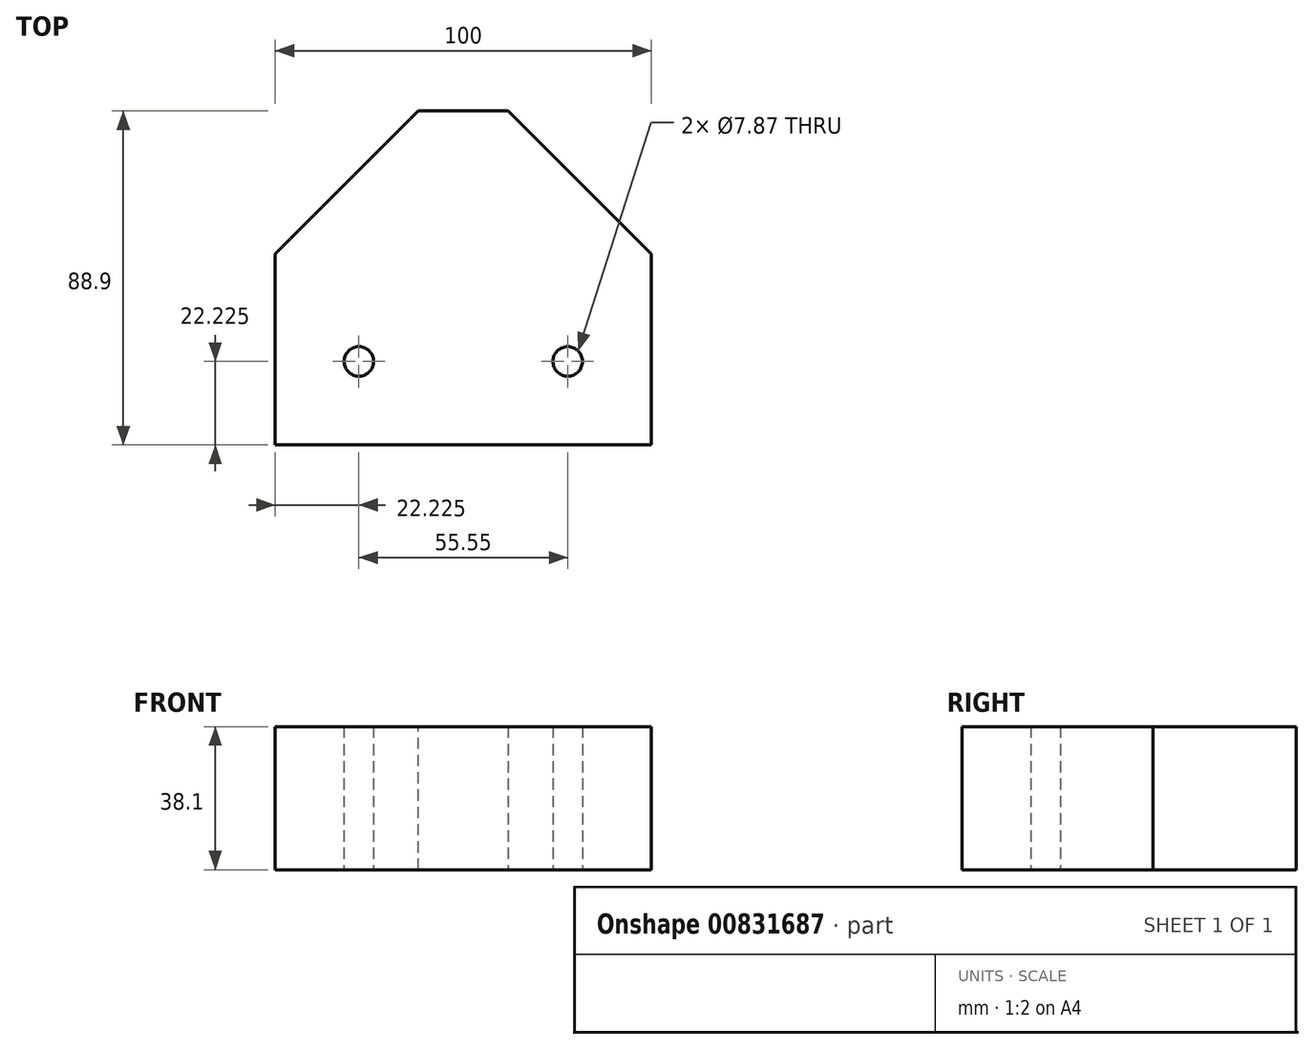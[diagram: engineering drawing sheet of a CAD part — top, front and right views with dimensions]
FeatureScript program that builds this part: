
annotation { "Feature Type Name" : "Feature", "Feature Type Description" : "" }
export const myFeature = defineFeature(function(context is Context, id is Id, definition is map)
    precondition{}
    {
        {
            var Q0;
            Q0=qCreatedBy(makeId("Top.planeOp"),FACE);
            var sketch = newSketch(context, id + "F0", { "sketchPlane" : qUnion([Q0])});
            skLineSegment(sketch, "E0.bottom", {"start": v(-50, 44.45) * mm, "end": v(50, 44.45) * mm});
            skLineSegment(sketch, "E0.top", {"start": v(-50, -44.45) * mm, "end": v(50, -44.45) * mm});
            skLineSegment(sketch, "E0.left", {"start": v(-50, 44.45) * mm, "end": v(-50, -44.45) * mm});
            skLineSegment(sketch, "E0.right", {"start": v(50, 44.45) * mm, "end": v(50, -44.45) * mm});
            skSolve(sketch);
        }
        {
            var Q0;
            Q0=makeQuery(id+"F0.imprint","IMPRINT",FACE,{"disambiguationData":[TD([[makeQuery(id+"F0.imprint","IMPRINT",EDGE,{"derivedFrom":sQuery(id+"F0.wireOp",EDGE,"E0.bottom")}),-1.0]])]});
            extrude(context, id + "F1", {"entities" : qUnion([Q0]), "depth" : 38.1 * mm, "offsetDistance" : 25.4 * mm});
        }
        {
            var Q0;
            Q0=makeQuery(id+"F1.opExtrude","SWEPT_EDGE",EDGE,{"disambiguationData":[OSD([sQuery(id+"F0.wireOp",EDGE,"E0.bottom"),sQuery(id+"F0.wireOp",EDGE,"E0.right")])]});
            var Q1;
            Q1=makeQuery(id+"F1.opExtrude","SWEPT_EDGE",EDGE,{"disambiguationData":[OSD([sQuery(id+"F0.wireOp",EDGE,"E0.bottom"),sQuery(id+"F0.wireOp",EDGE,"E0.left")])]});
            chamfer(context, id + "F2", {"entities" : qUnion([Q0, Q1]), "width" : 38.1 * mm, "tangentPropagation" : true});
        }
        {
            var Q0;
            Q0=makeQuery(id+"F1.opExtrude","CAP_FACE",FACE,{"disambiguationData":[OSD([sQuery(id+"F0.wireOp",EDGE,"E0.bottom"),sQuery(id+"F0.wireOp",EDGE,"E0.top"),sQuery(id+"F0.wireOp",EDGE,"E0.left"),sQuery(id+"F0.wireOp",EDGE,"E0.right")])],"isStart":true});
            var sketch = newSketch(context, id + "F3", { "sketchPlane" : qUnion([Q0])});
            skPoint(sketch, "E1", {"position": v(-27.78, 22.22) * mm});
            skPoint(sketch, "E2", {"position": v(27.78, 22.22) * mm});
            skSolve(sketch);
        }
        {
            var Q0;
            Q0=sQuery(id+"F3.wireOp",VERTEX,"E1");
            var Q1;
            Q1=sQuery(id+"F3.wireOp",VERTEX,"E2");
            var Q2;
            Q2=makeQuery(id+"F1.opExtrude","SWEPT_BODY",BODY,{"disambiguationData":[OSD([sQuery(id+"F0.wireOp",EDGE,"E0.bottom"),sQuery(id+"F0.wireOp",EDGE,"E0.top"),sQuery(id+"F0.wireOp",EDGE,"E0.left"),sQuery(id+"F0.wireOp",EDGE,"E0.right")])]});
            hole(context, id + "F4", {"style" : HoleStyle.SIMPLE, "endStyle" : HoleEndStyle.THROUGH, "holeDiameter" : 7.87 * mm, "majorDiameter" : 6.35 * mm, "isTappedThrough" : true, "tappedDepth" : 12.7 * mm, "tapClearance" : 3, "locations" : qUnion([Q0, Q1]), "scope" : qUnion([Q2])});
        }
    });
